# Revit family: NBS_COBAAfrica_EntMatt_Q-Beez
name_source: partatom
category: Generic Models
revit_build: Autodesk Revit 2018 (Build: 20190510_1515(x64)
units: mm (PartAtom-declared; Revit-internal decimal feet)

## family parameters
Can host rebar = No
Cut with Voids When Loaded = No
Host = Face
Part Type = Normal
Room Calculation Point = No
Round Connector Dimension = Use Diameter
Shared = No

## types (1)
- 2000x500mm
    ArrangementOptions = Suitable for dry indoor environments. Recessed only, adhered or loose lay
    AssetType = Fixed
    BIMObjectName = NBS_COBAAfrica_EntranceMatting_Q-Beez
    BaseColour = Black
    CarpetColourOptions = Grey, Anthracite
    Combustible = No
    Construction = Closed
    Default Elevation = 1200 mm
    Description = Hardwearing PVC Interlocking tile modules
    EdgingMaterial = NBS_Concept
    EntranceMattingHeight = 13 mm
    EntranceMattingLength = 500 mm  [stored 1.64042 ft]
    EntranceMattingMaterial = NBS_Concept
    EntranceMattingWidth = 2000 mm  [stored 6.56168 ft]
    ExpectedLife = 5 years plus if used in the correct environment for the volume and type of traffic as per specification
    FireRating = Cfi-S1
    HasAntiStaticSurface = No
    HasNonSkidSurface = Yes
    IfcExportAs = IfcCoveringType
    IfcExportType = FLOORING
    IsExternal = No
    ManufacturerName = COBA Africa
    ManufacturerURL = www.cobaafrica.com
    Material = 100% Polypropylene needlepunch with Tuft Polyamide surface finish
    MattingHeight = 13 mm
    ModelNumber = QB
    ModelReference = Q--Beez
    NBSDescription = Entrance matting
    NBSReference = 45-35-35/420
    Name = EntMatt_Q-Beez_COBAAfrica
    NominalHeight = 13 mm
    NominalLength = 500 mm  [stored 1.64042 ft]
    NominalWidth = 2000 mm  [stored 6.56168 ft]
    Pattern = Striped design
    ProductInformation = https://www.matting.co.za
    ThermalTransmittance = 0
    TrafficType = Pedestrian, wheel chairs, pushchairs and trolleys
    Uniclass2015Code = Pr_35_57_11_26
    Uniclass2015Title = Entrance mats
    Uniclass2015Version = Products v1.15
    Version = 1
    WarrantyDurationParts = n/a (dependent on application)
    WarrantyDurationUnit = year

note: [stored X ft] marks values corroborated as IEEE doubles in the binary element streams (Revit-internal decimal feet)

## geometry (parser evidence)
native form markers: Sweep x2
no freeform markers — native parametric forms only
